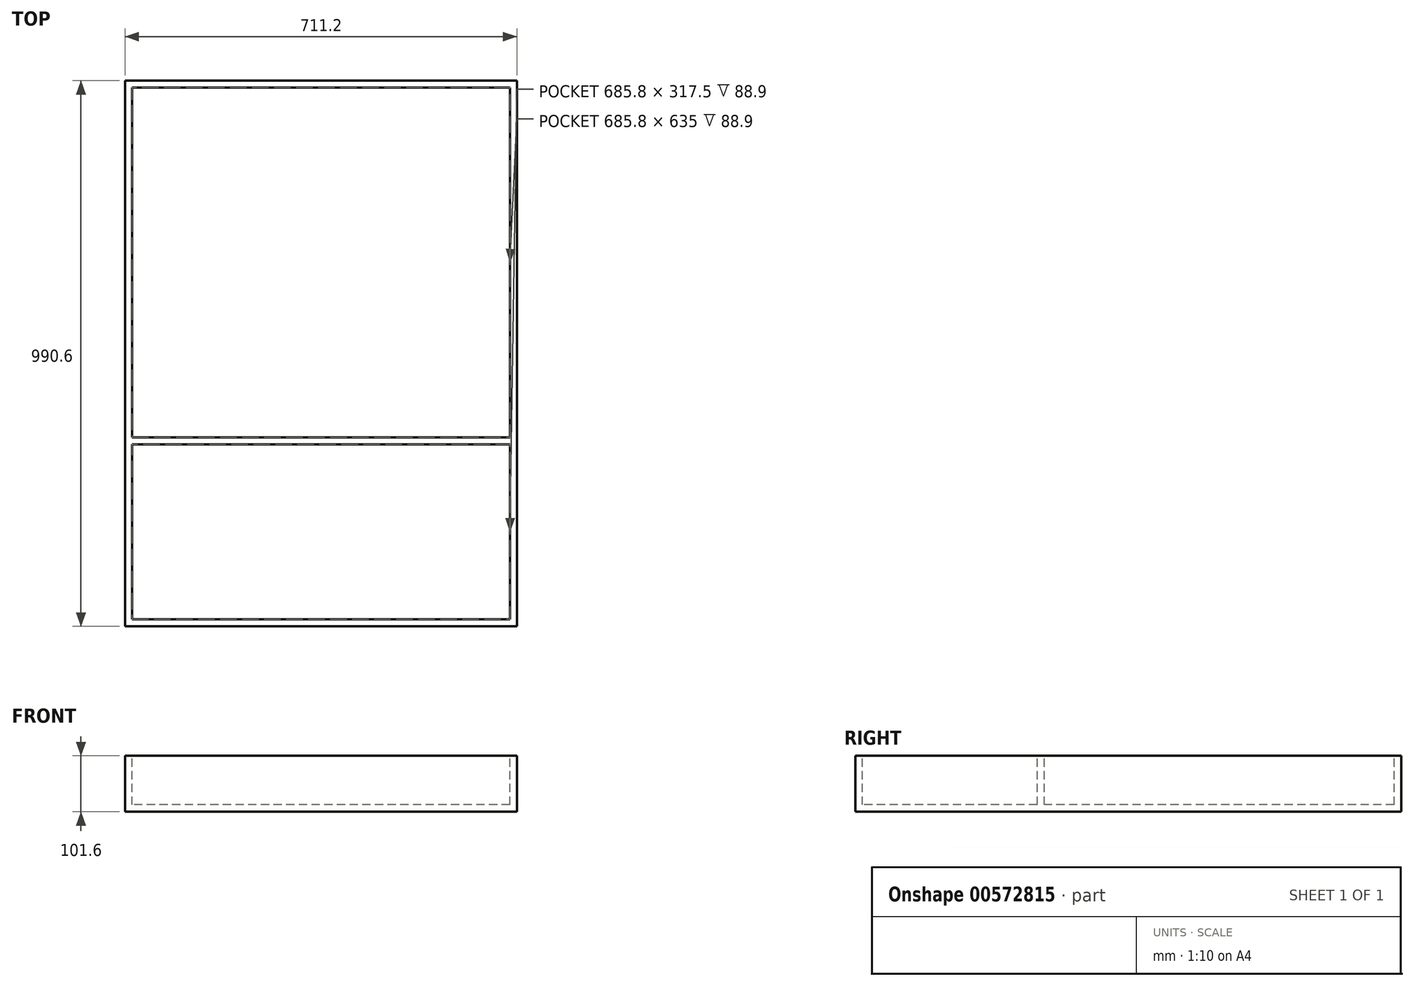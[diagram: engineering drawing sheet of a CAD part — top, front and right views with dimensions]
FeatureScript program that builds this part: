
annotation { "Feature Type Name" : "Feature", "Feature Type Description" : "" }
export const myFeature = defineFeature(function(context is Context, id is Id, definition is map)
    precondition{}
    {
        {
            var Q0;
            Q0=qCreatedBy(makeId("Top.planeOp"),FACE);
            var sketch = newSketch(context, id + "F0", { "sketchPlane" : qUnion([Q0])});
            skLineSegment(sketch, "E0.bottom", {"start": v(-342.9, -482.6) * mm, "end": v(342.9, -482.6) * mm});
            skLineSegment(sketch, "E0.top", {"start": v(-342.9, 482.6) * mm, "end": v(342.9, 482.6) * mm});
            skLineSegment(sketch, "E0.left", {"start": v(-342.9, -482.6) * mm, "end": v(-342.9, 482.6) * mm});
            skLineSegment(sketch, "E0.right", {"start": v(342.9, -482.6) * mm, "end": v(342.9, 482.6) * mm});
            skLineSegment(sketch, "E1.0", {"start": v(355.6, -495.3) * mm, "end": v(355.6, 495.3) * mm});
            skLineSegment(sketch, "E1.1", {"start": v(-355.6, -495.3) * mm, "end": v(355.6, -495.3) * mm});
            skLineSegment(sketch, "E1.2", {"start": v(-355.6, -495.3) * mm, "end": v(-355.6, 495.3) * mm});
            skLineSegment(sketch, "E1.3", {"start": v(-355.6, 495.3) * mm, "end": v(355.6, 495.3) * mm});
            skLineSegment(sketch, "E2", {"start": v(-342.9, -152.4) * mm, "end": v(342.9, -152.4) * mm});
            skLineSegment(sketch, "E3", {"start": v(-342.9, -165.1) * mm, "end": v(342.9, -165.1) * mm});
            skSolve(sketch);
        }
        {
            var Q0;
            Q0=makeQuery(id+"F0.imprint","IMPRINT",FACE,{"disambiguationData":[TD([[makeQuery(id+"F0.imprint","IMPRINT",EDGE,{"derivedFrom":sQuery(id+"F0.wireOp",EDGE,"E0.bottom")}),-1.0]])]});
            var Q1;
            Q1=makeQuery(id+"F0.imprint","IMPRINT",FACE,{"disambiguationData":[TD([[makeQuery(id+"F0.imprint","IMPRINT",EDGE,{"derivedFrom":sQuery(id+"F0.wireOp",EDGE,"E0.bottom")}),1.0]])]});
            var Q2;
            {var subQ0=sQuery(id+"F0.wireOp",EDGE,"E0.top");Q2=makeQuery(id+"F0.imprint","IMPRINT",FACE,{"disambiguationData":[TD([[makeQuery(id+"F0.imprint","IMPRINT",EDGE,{"derivedFrom":subQ0}),-1.0]])]});}
            var Q3;
            {var subQ0=sQuery(id+"F0.wireOp",EDGE,"E2");Q3=makeQuery(id+"F0.imprint","IMPRINT",FACE,{"disambiguationData":[TD([[makeQuery(id+"F0.imprint","IMPRINT",EDGE,{"derivedFrom":subQ0}),-1.0]])]});}
            extrude(context, id + "F1", {"entities" : qUnion([Q0, Q1, Q2, Q3]), "oppositeDirection" : true, "depth" : 101.6 * mm, "offsetDistance" : 25.4 * mm});
        }
        {
            var Q0;
            {var subQ0=sQuery(id+"F0.wireOp",EDGE,"E0.top");Q0=makeQuery(id+"F0.imprint","IMPRINT",FACE,{"disambiguationData":[TD([[makeQuery(id+"F0.imprint","IMPRINT",EDGE,{"derivedFrom":subQ0}),-1.0]])]});}
            var Q1;
            {var subQ0=sQuery(id+"F0.wireOp",EDGE,"E0.bottom");Q1=makeQuery(id+"F0.imprint","IMPRINT",FACE,{"disambiguationData":[TD([[makeQuery(id+"F0.imprint","IMPRINT",EDGE,{"derivedFrom":subQ0}),1.0]])]});}
            var Q2;
            Q2=makeQuery(id+"F1.opExtrude","CAP_FACE",FACE,{"disambiguationData":[OSD([sQuery(id+"F0.wireOp",EDGE,"E0.left"),sQuery(id+"F0.wireOp",EDGE,"E0.right"),sQuery(id+"F0.wireOp",EDGE,"E1.0"),sQuery(id+"F0.wireOp",EDGE,"E1.1"),sQuery(id+"F0.wireOp",EDGE,"E1.2"),sQuery(id+"F0.wireOp",EDGE,"E1.3"),sQuery(id+"F0.wireOp",EDGE,"E2"),sQuery(id+"F0.wireOp",EDGE,"E3")])],"isStart":false});
            extrude(context, id + "F2", {"entities" : qUnion([Q0, Q1]), "operationType" : NewBodyOperationType.REMOVE, "endBound" : BoundingType.UP_TO_SURFACE, "oppositeDirection" : true, "depth" : 25.4 * mm, "endBoundEntityFace" : qUnion([Q2]), "hasOffset" : true, "offsetDistance" : 12.7 * mm});
        }
    });
